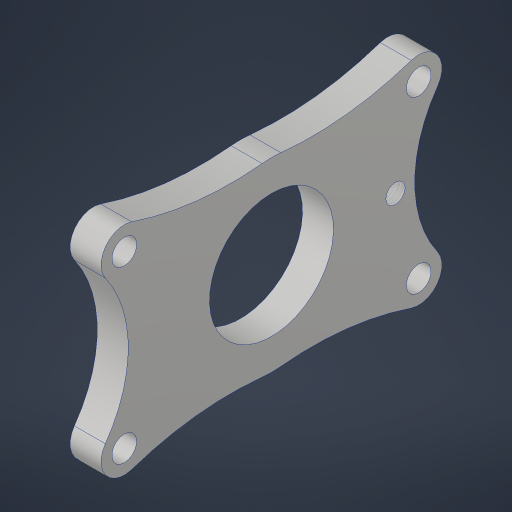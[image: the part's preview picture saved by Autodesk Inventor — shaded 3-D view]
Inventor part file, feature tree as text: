
AUTODESK INVENTOR PART (.ipt)
format: ipt  version: 2023.4 (Build 274418000, 418)  size: 216,576 bytes
history: native  units: in
note: dims shown in document units (in); Inventor stores cm internally (conversion verified against a paired STEP export)
features: hole x2, sketch x1, extrude x1
ambient origin geometry x8: Origin, YZ Plane, XZ Plane, XY Plane, X Axis, Y Axis, Z Axis, Center Point
bodies: Solid1 (feature_tree)
feature tree (4):
  sketch  "Sketch1"  dims[d1=1.375in d2=2.375in d3=1.0in d4=0.375in d5=1.0in d6=0.25in d7=2.5in d8=1.0in d9=0.25in d10=0.0in d11=0.201in d12=0.75in d13=0.385in d14=0.25in d15=0.5635in d16=1.0in d17=0.8108in d18=0.156in d19=0.38in d20=0.375in d21=0.25in d22=0.5635in d23=1.0in d24=0.8108in]
  extrude  "Extrusion1"  Depth=1.0in
  hole  "Hole1"  [1 undecoded]
  hole  "Hole2"  [1 undecoded]
note: 2 required parameter values undecoded (feature->parameter linkage not recoverable at this tier; creation-order binding heuristic only, values carry confidence <= 0.55)
